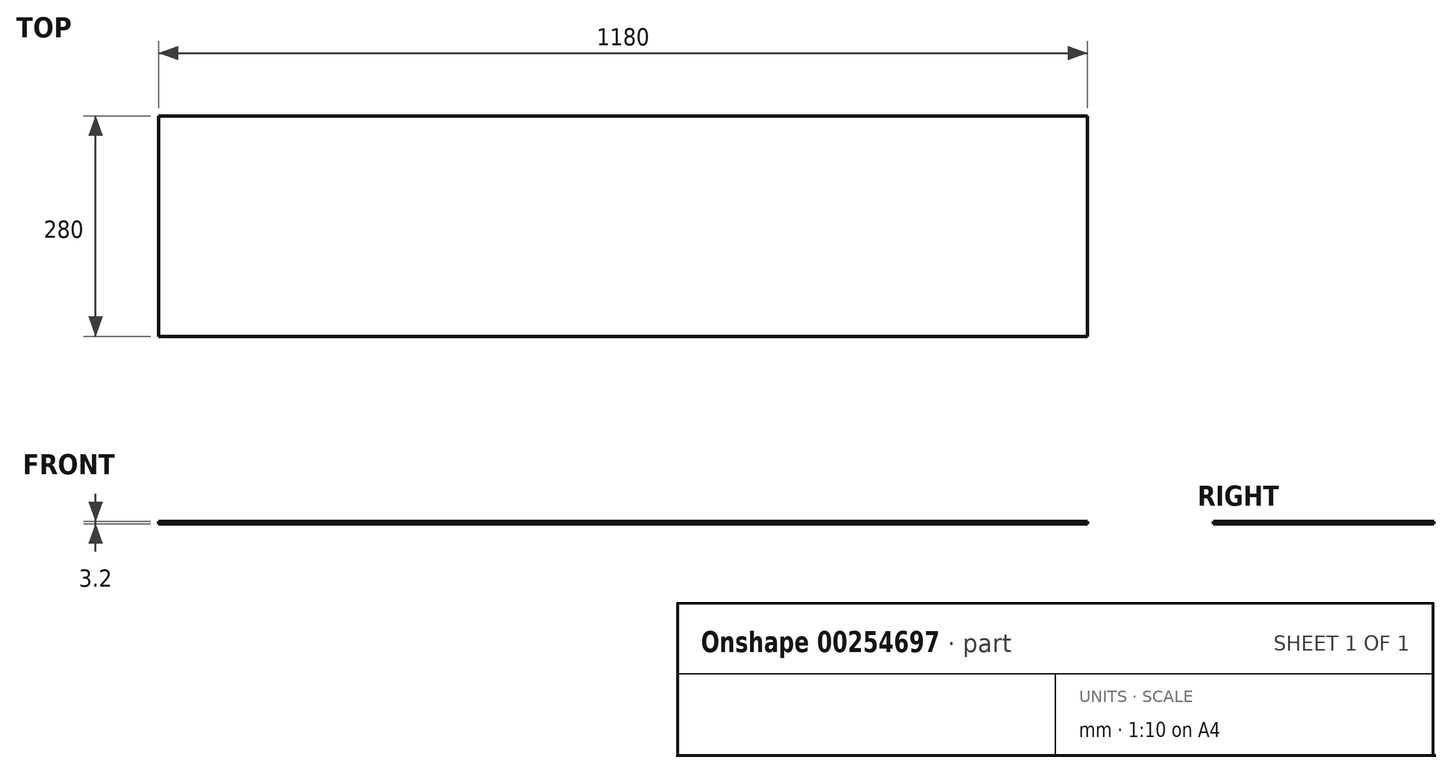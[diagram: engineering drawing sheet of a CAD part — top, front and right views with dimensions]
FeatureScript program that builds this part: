
annotation { "Feature Type Name" : "Feature", "Feature Type Description" : "" }
export const myFeature = defineFeature(function(context is Context, id is Id, definition is map)
    precondition{}
    {
        {
            var Q0;
            Q0=qCreatedBy(makeId("Top.planeOp"),FACE);
            var sketch = newSketch(context, id + "F0", { "sketchPlane" : qUnion([Q0])});
            skLineSegment(sketch, "E0.bottom", {"start": v(0, 0) * mm, "end": v(1180, 0) * mm});
            skLineSegment(sketch, "E0.top", {"start": v(0, 280) * mm, "end": v(1180, 280) * mm});
            skLineSegment(sketch, "E0.left", {"start": v(0, 0) * mm, "end": v(0, 280) * mm});
            skLineSegment(sketch, "E0.right", {"start": v(1180, 0) * mm, "end": v(1180, 280) * mm});
            skSolve(sketch);
        }
        {
            var Q0;
            Q0=qSketchRegion(id+"F0",true);
            extrude(context, id + "F1", {"entities" : qUnion([Q0]), "depth" : 3.2 * mm});
        }
    });
